# Revit family: Drain_Floor_Top_Square_10-Inch_Zurn-FD2283
name_source: partatom
category: Plumbing Fixtures
units: mm (PartAtom-declared; Revit-internal decimal feet)

## family parameters
Always vertical = Yes
Cut with Voids When Loaded = No
Maintain Annotation Orientation = No
OmniClass Number = 23.70.50.21.24.14
OmniClass Title = Deck Waste Water Drains
Part Type = Normal
Room Calculation Point = No
Round Connector Dimension = Use Radius
Shared = No
Work Plane-Based = No

## types (3) — shared parameters
Assembly Code = D2030300
Body Range = 2.375 "
CW Connection = No
Default Elevation = 25 "
Description = 10[254] Square Top Decorative Floor Drain
Grate Height = 0.188 "
Grate Open Area Sq.in = 23 "
HW Connection = No
Main Material = Polyvinyl Chloride - Zurn - Polished
Manufacturer = Zurn Water, LLC
Manufacurer Brand = Zurn
Model = FD2283
Modified Date = 10/31/2025
P-trap = 0.25 "
Product Documentation Link = https://files.zurn.com
Product Page URL = https://www.zurn.com
Product data url = https://www.bimobject.com
Square Top Decorative (SQ) = 10 "
URL = www.zurn.com
Vent Connection = No
WFU = 1
Waste Connection = Yes
Width = 8.875 "
zero-valued in all types: CWFU, HWFU

## per-type parameters (varying)
| type | Body Height (E) | Pipe Size A (Actual Radius) | Pipe Size A (Inner Radius) | Pipe Size A (Nominal Radius) |
| FD2283-PV2-2 Inch Outlet | 2.969 " | 1.188 " | 1.034 " | 1 " |
| FD2283-PV3-3 Inch Outlet | 3.688 " | 1.75 " | 1.534 " | 1.5 " |
| FD2283-PV4-4 Inch Outlet | 3.813 " | 2.25 " | 2.013 " | 2 " |

## geometry (parser evidence)
native form markers: Sweep x5
no freeform markers — native parametric forms only
